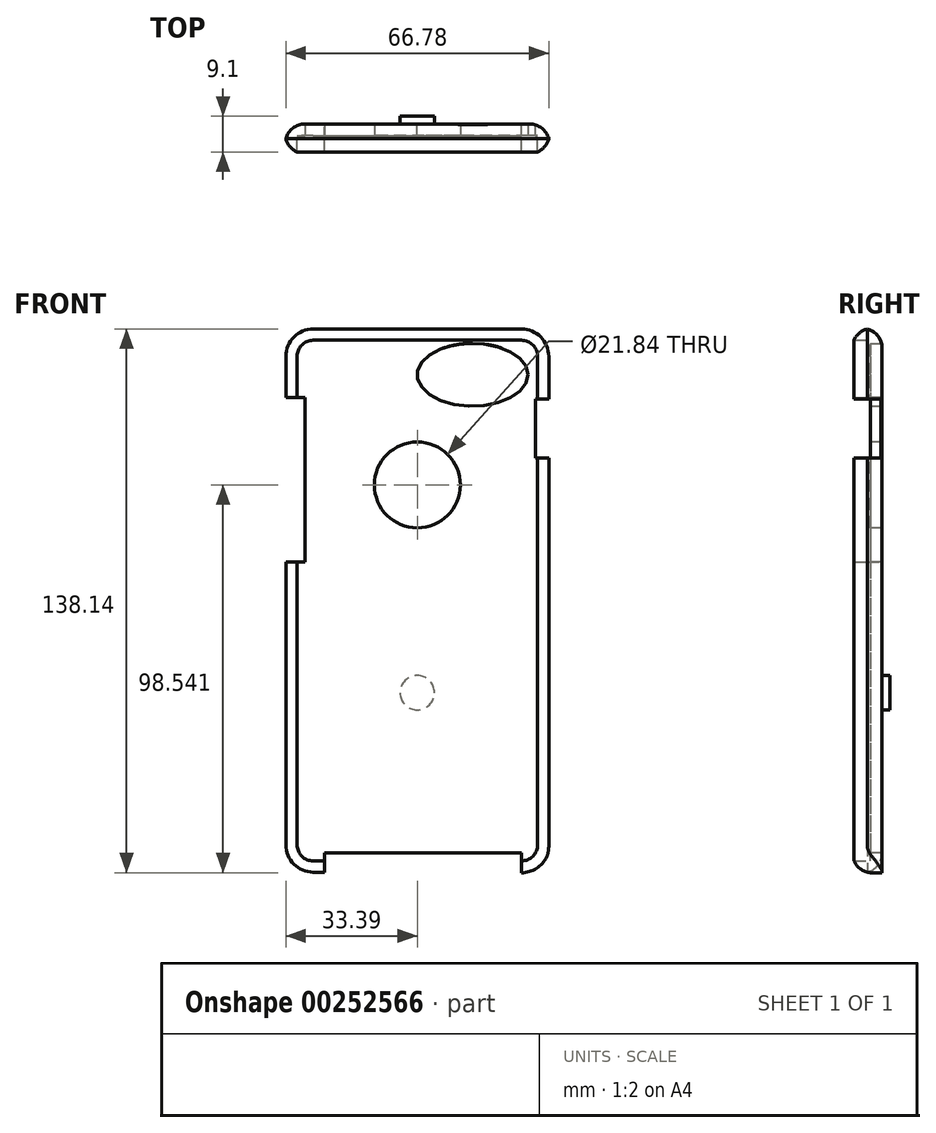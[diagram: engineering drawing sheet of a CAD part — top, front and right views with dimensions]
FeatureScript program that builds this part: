
annotation { "Feature Type Name" : "Feature", "Feature Type Description" : "" }
export const myFeature = defineFeature(function(context is Context, id is Id, definition is map)
    precondition{}
    {
        {
            var Q0;
            Q0=qCreatedBy(makeId("Front.planeOp"),FACE);
            var sketch = newSketch(context, id + "F0", { "sketchPlane" : qUnion([Q0])});
            skLineSegment(sketch, "E0.bottom", {"start": v(-33.55, 69.15) * mm, "end": v(33.55, 69.15) * mm});
            skLineSegment(sketch, "E0.top", {"start": v(-33.55, -69.15) * mm, "end": v(33.55, -69.15) * mm});
            skLineSegment(sketch, "E0.left", {"start": v(-33.55, 69.15) * mm, "end": v(-33.55, -69.15) * mm});
            skLineSegment(sketch, "E0.right", {"start": v(33.55, 69.15) * mm, "end": v(33.55, -69.15) * mm});
            skPoint(sketch, "E0.middle", {"position": v(0, 0) * mm});
            skSolve(sketch);
        }
        {
            var Q0;
            Q0=makeQuery(id+"F0.imprint","IMPRINT",FACE,{"disambiguationData":[TD([[makeQuery(id+"F0.imprint","IMPRINT",EDGE,{"derivedFrom":sQuery(id+"F0.wireOp",EDGE,"E0.bottom")}),-1.0]])]});
            extrude(context, id + "F1", {"entities" : qUnion([Q0]), "depth" : 7.1 * mm});
        }
        {
            var Q0;
            Q0=makeQuery(id+"F1.opExtrude","SWEPT_EDGE",EDGE,{"disambiguationData":[OSD([sQuery(id+"F0.wireOp",EDGE,"E0.bottom"),sQuery(id+"F0.wireOp",EDGE,"E0.right")])]});
            var Q1;
            Q1=makeQuery(id+"F1.opExtrude","SWEPT_EDGE",EDGE,{"disambiguationData":[OSD([sQuery(id+"F0.wireOp",EDGE,"E0.top"),sQuery(id+"F0.wireOp",EDGE,"E0.left")])]});
            var Q2;
            Q2=makeQuery(id+"F1.opExtrude","SWEPT_EDGE",EDGE,{"disambiguationData":[OSD([sQuery(id+"F0.wireOp",EDGE,"E0.top"),sQuery(id+"F0.wireOp",EDGE,"E0.right")])]});
            var Q3;
            Q3=makeQuery(id+"F1.opExtrude","SWEPT_EDGE",EDGE,{"disambiguationData":[OSD([sQuery(id+"F0.wireOp",EDGE,"E0.bottom"),sQuery(id+"F0.wireOp",EDGE,"E0.left")])]});
            fillet(context, id + "F2", {"entities" : qUnion([Q0, Q1, Q2, Q3]), "radius" : 7.1 * mm, "tangentPropagation" : true, "allowEdgeOverflow" : false});
        }
        {
            var Q0;
            Q0=makeQuery(id+"F1.opExtrude","CAP_FACE",FACE,{"disambiguationData":[OSD([sQuery(id+"F0.wireOp",EDGE,"E0.bottom"),sQuery(id+"F0.wireOp",EDGE,"E0.top"),sQuery(id+"F0.wireOp",EDGE,"E0.left"),sQuery(id+"F0.wireOp",EDGE,"E0.right")])],"isStart":false});
            shell(context, id + "F3", {"entities" : qUnion([Q0]), "thickness" : 3 * mm});
        }
        {
            var Q0;
            Q0=makeQuery(id+"F3.opShell","OFFSET_FACE",FACE,{"disambiguationData":[OSD([sQuery(id+"F0.wireOp",EDGE,"E0.bottom"),sQuery(id+"F0.wireOp",EDGE,"E0.top"),sQuery(id+"F0.wireOp",EDGE,"E0.left"),sQuery(id+"F0.wireOp",EDGE,"E0.right")])]});
            var sketch = newSketch(context, id + "F4", { "sketchPlane" : qUnion([Q0])});
            skEllipse(sketch, "E1", {"center": v(14.06, 57.39) * mm, "majorRadius": 14.1 * mm, "minorRadius": 7.98 * mm, "majorAxis": v(1, 0)});
            skCircle(sketch, "E2", {"center": v(0, 29.4) * mm, "radius": 10.92 * mm});
            skSolve(sketch);
        }
        {
            var Q0;
            Q0=makeQuery(id+"F4.imprint","IMPRINT",FACE,{"disambiguationData":[TD([[makeQuery(id+"F4.imprint","IMPRINT",EDGE,{"derivedFrom":sQuery(id+"F4.wireOp",EDGE,"E1")}),1.0]])]});
            var Q1;
            Q1=makeQuery(id+"F4.imprint","IMPRINT",FACE,{"disambiguationData":[TD([[makeQuery(id+"F4.imprint","IMPRINT",EDGE,{"derivedFrom":sQuery(id+"F4.wireOp",EDGE,"E2")}),1.0]])]});
            extrude(context, id + "F5", {"entities" : qUnion([Q0, Q1]), "operationType" : NewBodyOperationType.REMOVE, "endBound" : BoundingType.SYMMETRIC, "oppositeDirection" : true, "depth" : 25 * mm});
        }
        {
            var Q0;
            Q0=makeQuery(id+"F1.opExtrude","SWEPT_FACE",FACE,{"disambiguationData":[OSD([sQuery(id+"F0.wireOp",EDGE,"E0.top")])]});
            var sketch = newSketch(context, id + "F6", { "sketchPlane" : qUnion([Q0])});
            skLineSegment(sketch, "E3.bottom", {"start": v(-23.53, 0) * mm, "end": v(26.45, 0) * mm});
            skLineSegment(sketch, "E3.top", {"start": v(-23.53, 7.1) * mm, "end": v(26.45, 7.1) * mm});
            skLineSegment(sketch, "E3.left", {"start": v(-23.53, 0) * mm, "end": v(-23.53, 7.1) * mm});
            skLineSegment(sketch, "E3.right", {"start": v(26.45, 0) * mm, "end": v(26.45, 7.1) * mm});
            skLineSegment(sketch, "E4.bottom", {"start": v(-23.53, 7.1) * mm, "end": v(-26.45, 7.1) * mm});
            skLineSegment(sketch, "E4.top", {"start": v(-23.53, 7.1) * mm, "end": v(-26.45, 7.1) * mm});
            skLineSegment(sketch, "E4.left", {"start": v(-23.53, 7.1) * mm, "end": v(-23.53, 7.1) * mm});
            skLineSegment(sketch, "E4.right", {"start": v(-26.45, 7.1) * mm, "end": v(-26.45, 7.1) * mm});
            skSolve(sketch);
        }
        {
            var Q0;
            Q0=makeQuery(id+"F6.imprint","IMPRINT",FACE,{"disambiguationData":[TD([[makeQuery(id+"F6.imprint","IMPRINT",EDGE,{"derivedFrom":sQuery(id+"F6.wireOp",EDGE,"E3.bottom")}),1.0]])]});
            extrude(context, id + "F7", {"entities" : qUnion([Q0]), "operationType" : NewBodyOperationType.REMOVE, "endBound" : BoundingType.SYMMETRIC, "oppositeDirection" : true, "depth" : 10 * mm});
        }
        {
            var Q0;
            Q0=makeQuery(id+"F1.opExtrude","SWEPT_FACE",FACE,{"disambiguationData":[OSD([sQuery(id+"F0.wireOp",EDGE,"E0.left")])]});
            var sketch = newSketch(context, id + "F8", { "sketchPlane" : qUnion([Q0])});
            skLineSegment(sketch, "E5.bottom", {"start": v(0, 51.55) * mm, "end": v(7.1, 51.55) * mm});
            skLineSegment(sketch, "E5.top", {"start": v(0, 9.8) * mm, "end": v(7.1, 9.8) * mm});
            skLineSegment(sketch, "E5.left", {"start": v(0, 51.55) * mm, "end": v(0, 9.8) * mm});
            skLineSegment(sketch, "E5.right", {"start": v(7.1, 51.55) * mm, "end": v(7.1, 9.8) * mm});
            skSolve(sketch);
        }
        {
            var Q0;
            Q0=makeQuery(id+"F8.imprint","IMPRINT",FACE,{"disambiguationData":[TD([[makeQuery(id+"F8.imprint","IMPRINT",EDGE,{"derivedFrom":sQuery(id+"F8.wireOp",EDGE,"E5.bottom")}),-1.0]])]});
            extrude(context, id + "F9", {"entities" : qUnion([Q0]), "operationType" : NewBodyOperationType.REMOVE, "endBound" : BoundingType.SYMMETRIC, "oppositeDirection" : true, "depth" : 10 * mm});
        }
        {
            var Q0;
            Q0=makeQuery(id+"F1.opExtrude","SWEPT_FACE",FACE,{"disambiguationData":[OSD([sQuery(id+"F0.wireOp",EDGE,"E0.right")])]});
            var sketch = newSketch(context, id + "F10", { "sketchPlane" : qUnion([Q0])});
            skLineSegment(sketch, "E6.bottom", {"start": v(-7.1, 51.21) * mm, "end": v(0, 51.21) * mm});
            skLineSegment(sketch, "E6.top", {"start": v(-7.1, 36.21) * mm, "end": v(0, 36.21) * mm});
            skLineSegment(sketch, "E6.left", {"start": v(-7.1, 51.21) * mm, "end": v(-7.1, 36.21) * mm});
            skLineSegment(sketch, "E6.right", {"start": v(0, 51.21) * mm, "end": v(0, 36.21) * mm});
            skSolve(sketch);
        }
        {
            var Q0;
            Q0=makeQuery(id+"F10.imprint","IMPRINT",FACE,{"disambiguationData":[TD([[makeQuery(id+"F10.imprint","IMPRINT",EDGE,{"derivedFrom":sQuery(id+"F10.wireOp",EDGE,"E6.bottom")}),-1.0]])]});
            extrude(context, id + "F11", {"entities" : qUnion([Q0]), "operationType" : NewBodyOperationType.REMOVE, "endBound" : BoundingType.SYMMETRIC, "oppositeDirection" : true, "depth" : 7 * mm});
        }
        {
            var Q0;
            {var subQ0=sQuery(id+"F0.wireOp",EDGE,"E0.left");var subQ1=sQuery(id+"F0.wireOp",EDGE,"E0.bottom");Q0=makeQuery(id+"F2.opFillet","BLEND_EDGE",EDGE,{"blendedFrom":[makeQuery(id+"F1.opExtrude","SWEPT_EDGE",EDGE,{"disambiguationData":[OSD([subQ1,subQ0])]}),makeQuery(id+"F1.opExtrude","CAP_FACE",FACE,{"disambiguationData":[OSD([subQ1,sQuery(id+"F0.wireOp",EDGE,"E0.top"),subQ0,sQuery(id+"F0.wireOp",EDGE,"E0.right")])],"isStart":false})],"blendedInto":[makeQuery(id+"F1.opExtrude","CAP_FACE",FACE,{"disambiguationData":[OSD([subQ1,sQuery(id+"F0.wireOp",EDGE,"E0.top"),subQ0,sQuery(id+"F0.wireOp",EDGE,"E0.right")])],"isStart":false})]});}
            var Q1;
            {var subQ0=sQuery(id+"F0.wireOp",EDGE,"E0.left");Q1=makeQuery(id+"F9.boolean.opBoolean","SPLIT",EDGE,{"disambiguationData":[TD([makeQuery(id+"F9.opExtrude","SWEPT_FACE",FACE,{"disambiguationData":[OSD([sQuery(id+"F8.wireOp",EDGE,"E5.bottom")])]})])],"derivedFrom":makeQuery(id+"F1.opExtrude","CAP_EDGE",EDGE,{"disambiguationData":[OSD([subQ0])],"isStart":true})});}
            var Q2;
            Q2=makeQuery(id+"F9.boolean.opBoolean","COPY",EDGE,{"derivedFrom":makeQuery(id+"F9.opExtrude","CAP_EDGE",EDGE,{"disambiguationData":[OSD([sQuery(id+"F8.wireOp",EDGE,"E5.left")])],"isStart":false})});
            var Q3;
            {var subQ0=sQuery(id+"F0.wireOp",EDGE,"E0.left");Q3=makeQuery(id+"F9.boolean.opBoolean","SPLIT",EDGE,{"disambiguationData":[TD([makeQuery(id+"F9.opExtrude","SWEPT_FACE",FACE,{"disambiguationData":[OSD([sQuery(id+"F8.wireOp",EDGE,"E5.top")])]})])],"derivedFrom":makeQuery(id+"F1.opExtrude","CAP_EDGE",EDGE,{"disambiguationData":[OSD([subQ0])],"isStart":true})});}
            var Q4;
            {var subQ0=sQuery(id+"F0.wireOp",EDGE,"E0.left");Q4=makeQuery(id+"F9.boolean.opBoolean","SPLIT",EDGE,{"disambiguationData":[TD([makeQuery(id+"F9.opExtrude","SWEPT_FACE",FACE,{"disambiguationData":[OSD([sQuery(id+"F8.wireOp",EDGE,"E5.top")])]})])],"derivedFrom":makeQuery(id+"F1.opExtrude","CAP_EDGE",EDGE,{"disambiguationData":[OSD([subQ0])],"isStart":false})});}
            var Q5;
            {var subQ0=sQuery(id+"F0.wireOp",EDGE,"E0.right");var subQ1=sQuery(id+"F0.wireOp",EDGE,"E0.top");Q5=makeQuery(id+"F2.opFillet","BLEND_EDGE",EDGE,{"blendedFrom":[makeQuery(id+"F1.opExtrude","SWEPT_EDGE",EDGE,{"disambiguationData":[OSD([subQ1,subQ0])]}),makeQuery(id+"F1.opExtrude","CAP_FACE",FACE,{"disambiguationData":[OSD([sQuery(id+"F0.wireOp",EDGE,"E0.bottom"),subQ1,sQuery(id+"F0.wireOp",EDGE,"E0.left"),subQ0])],"isStart":false})],"blendedInto":[makeQuery(id+"F1.opExtrude","CAP_FACE",FACE,{"disambiguationData":[OSD([sQuery(id+"F0.wireOp",EDGE,"E0.bottom"),subQ1,sQuery(id+"F0.wireOp",EDGE,"E0.left"),subQ0])],"isStart":false})]});}
            fillet(context, id + "F12", {"entities" : qUnion([Q0, Q1, Q2, Q3, Q4, Q5]), "radius" : 5 * mm, "tangentPropagation" : true, "allowEdgeOverflow" : false});
        }
        {
            var Q0;
            Q0=qCreatedBy(makeId("Front.planeOp"),FACE);
            var sketch = newSketch(context, id + "F13", { "sketchPlane" : qUnion([Q0])});
            skCircle(sketch, "E7", {"center": v(0, -23.41) * mm, "radius": 4.36 * mm});
            skSolve(sketch);
        }
        {
            var Q0;
            Q0=makeQuery(id+"F13.imprint","IMPRINT",FACE,{"disambiguationData":[TD([[makeQuery(id+"F13.imprint","IMPRINT",EDGE,{"derivedFrom":sQuery(id+"F13.wireOp",EDGE,"E7")}),1.0]])]});
            extrude(context, id + "F14", {"entities" : qUnion([Q0]), "operationType" : NewBodyOperationType.ADD, "oppositeDirection" : true, "depth" : 2 * mm});
        }
    });
